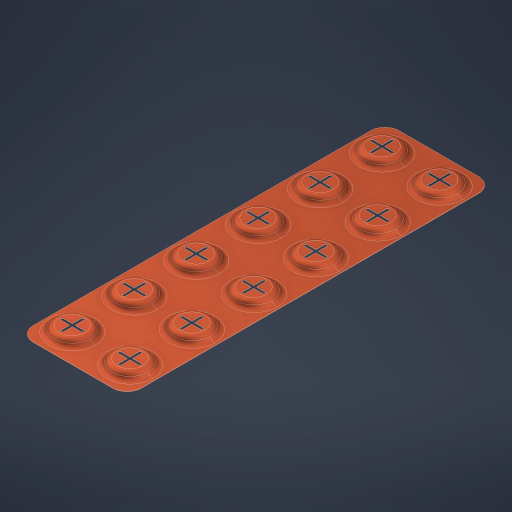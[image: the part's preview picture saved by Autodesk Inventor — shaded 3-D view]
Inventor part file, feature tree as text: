
AUTODESK INVENTOR PART (.ipt)
format: ipt  version: 2024.3 (Build 283343010, 343A)  size: 912,384 bytes
history: native  units: mm
features: sketch x2, extrude x2, fillet x1, pattern_linear x1, shell x1, other x1
ambient origin geometry x8: Origin, YZ Plane, XZ Plane, XY Plane, X Axis, Y Axis, Z Axis, Center Point
bodies: Volumenkörper1 (feature_tree)
feature tree (8):
  sketch  "Skizze1"  dims[d0=10.0mm d1=10.0mm]
  extrude  "Extrusion1"  Depth=10.0mm
  extrude  "Extrusion2"  Depth=0.5mm
  fillet  "Rundung1"  Radius=9.75mm
  pattern_linear  "Rechteckige Anordnung1"  Spacing1=8.75mm  [1 undecoded]
  shell  "Wandung1"  Thickness=8.75mm
  sketch  "Skizze2"  dims[d2=20.0mm d4=20.0mm d5=60.0mm d7=21.5mm d11=9.75mm d12=9.75mm d13=8.75mm d14=8.75mm d15=20.0mm d16=1.0mm d17=7.0mm d18=8.75mm d19=20.0mm d21=20.0mm d22=60.0mm d24=21.5mm d27=5.0mm d28=8.75mm d29=10.0mm d30=0.0mm d32=13.0mm d33=2.1mm d34=0.0mm d35=2.0mm d36=20.0mm d38=20.0mm d39=60.0mm d41=21.5mm d42=0.15mm d43=0.5mm d44=0.5mm d45=0.0mm]
  other  "Ausschneiden1"
note: 1 required parameter value undecoded (feature->parameter linkage not recoverable at this tier; creation-order binding heuristic only, values carry confidence <= 0.55)
